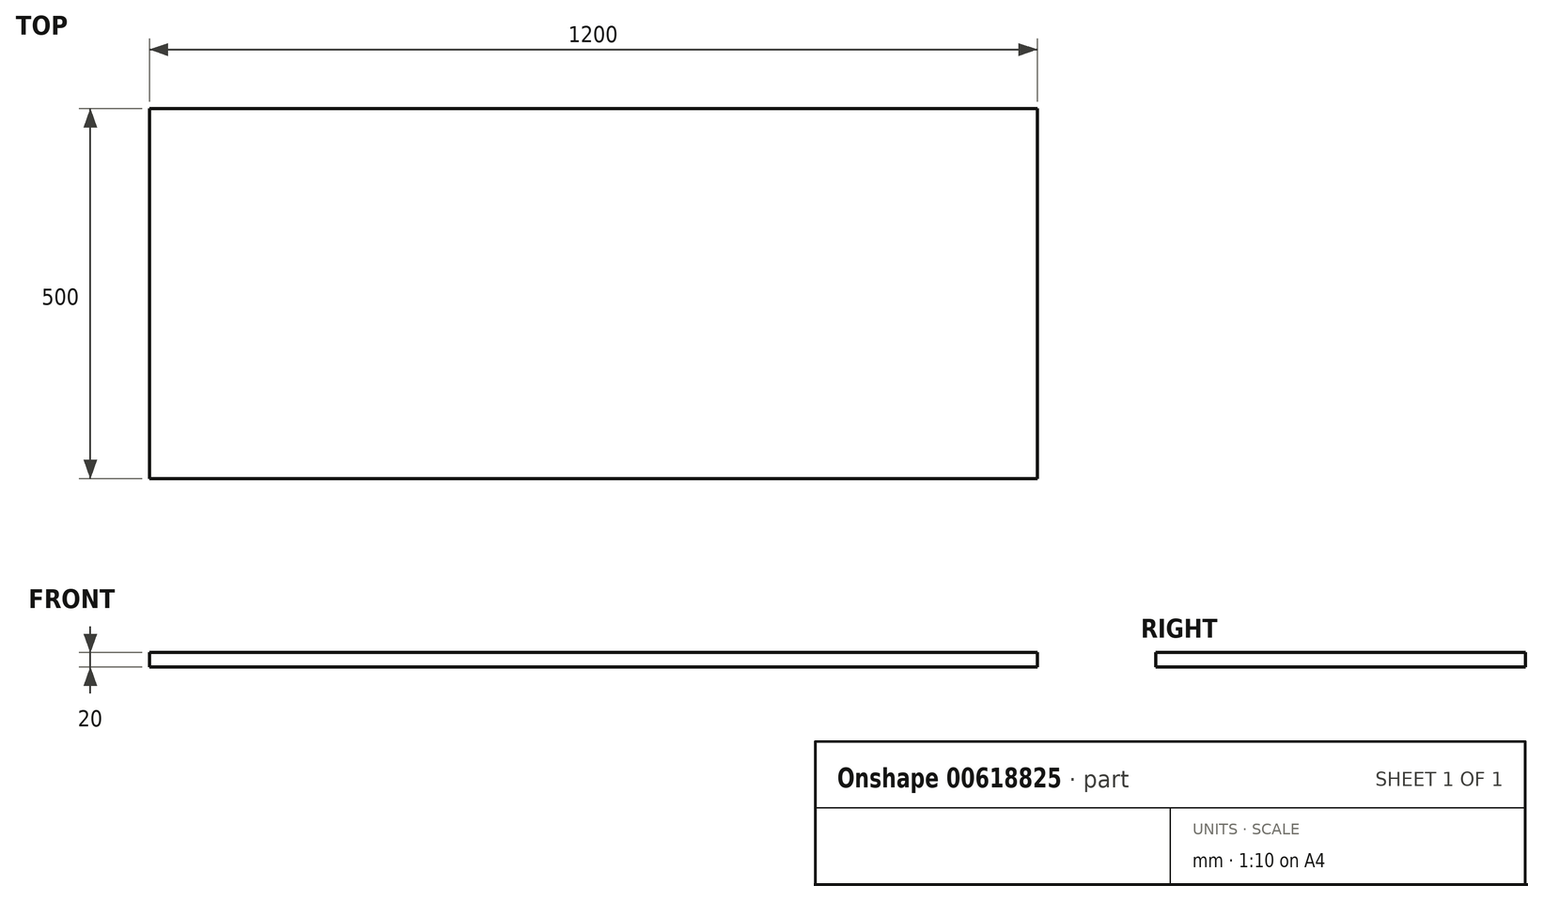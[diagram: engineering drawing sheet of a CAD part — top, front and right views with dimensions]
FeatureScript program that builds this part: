
annotation { "Feature Type Name" : "Feature", "Feature Type Description" : "" }
export const myFeature = defineFeature(function(context is Context, id is Id, definition is map)
    precondition{}
    {
        {
            var Q0;
            Q0=qCreatedBy(makeId("Top.planeOp"),FACE);
            var sketch = newSketch(context, id + "F0", { "sketchPlane" : qUnion([Q0])});
            skLineSegment(sketch, "E0.bottom", {"start": v(600, 250) * mm, "end": v(-600, 250) * mm});
            skLineSegment(sketch, "E0.top", {"start": v(600, -250) * mm, "end": v(-600, -250) * mm});
            skLineSegment(sketch, "E0.left", {"start": v(600, 250) * mm, "end": v(600, -250) * mm});
            skLineSegment(sketch, "E0.right", {"start": v(-600, 250) * mm, "end": v(-600, -250) * mm});
            skPoint(sketch, "E0.middle", {"position": v(0, 0) * mm});
            skSolve(sketch);
        }
        {
            var Q0;
            Q0=qSketchRegion(id+"F0",true);
            extrude(context, id + "F1", {"entities" : qUnion([Q0]), "depth" : 20 * mm, "offsetDistance" : 25.4 * mm});
        }
    });
